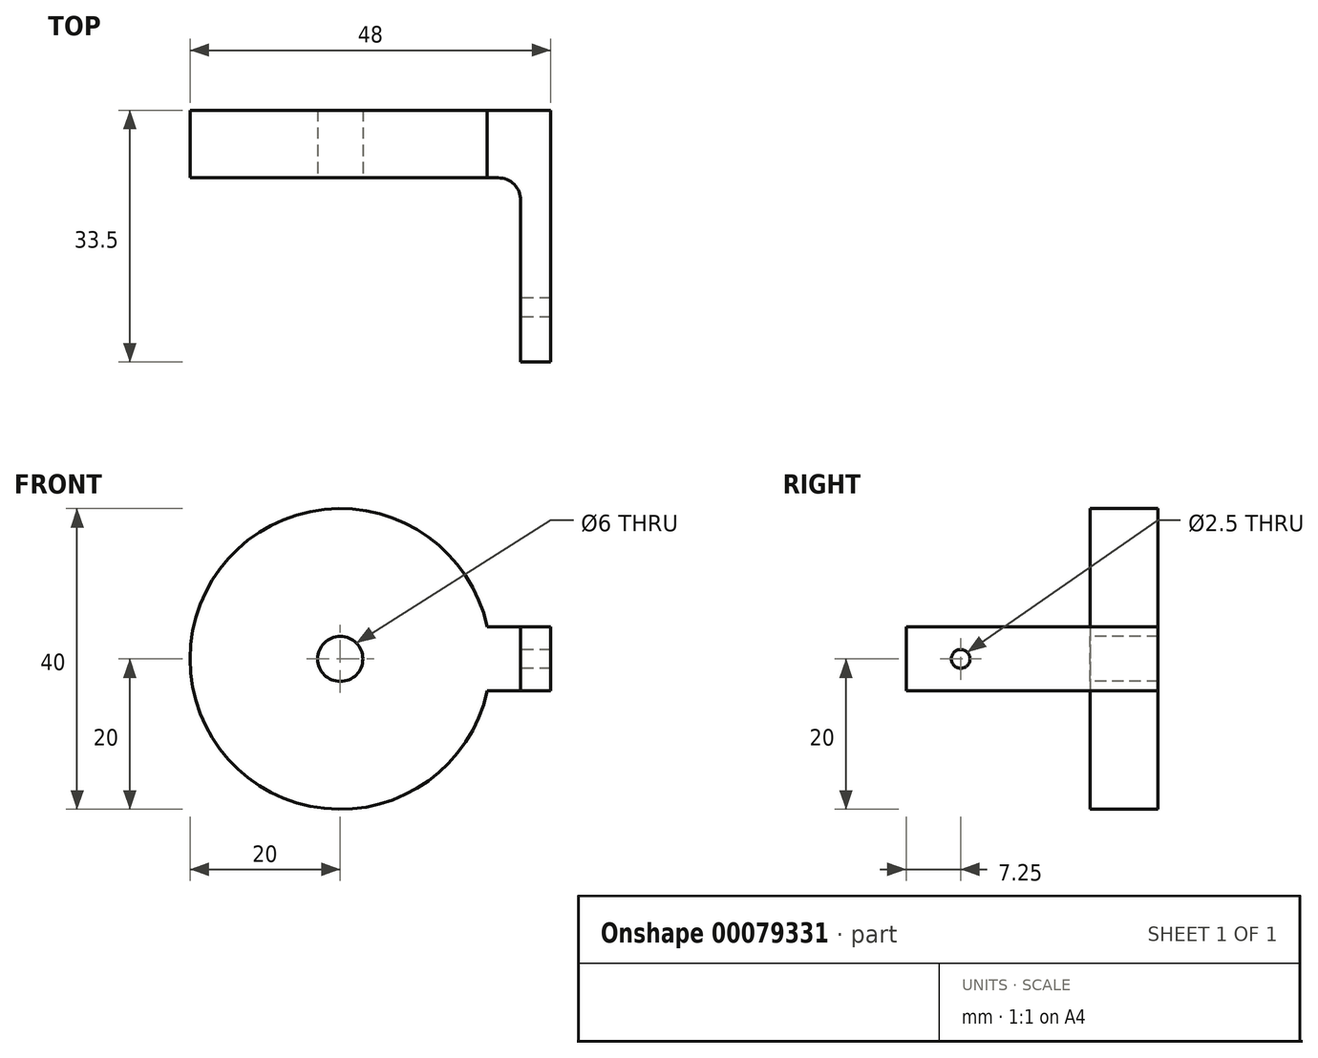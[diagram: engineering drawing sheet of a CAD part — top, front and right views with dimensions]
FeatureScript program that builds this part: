
annotation { "Feature Type Name" : "Feature", "Feature Type Description" : "" }
export const myFeature = defineFeature(function(context is Context, id is Id, definition is map)
    precondition{}
    {
        {
            var Q0;
            Q0=qCreatedBy(makeId("Front.planeOp"),FACE);
            var sketch = newSketch(context, id + "F0", { "sketchPlane" : qUnion([Q0])});
            skCircle(sketch, "E0", {"center": v(0, 0) * mm, "radius": 20 * mm});
            skSolve(sketch);
        }
        {
            var Q0;
            Q0 = qSketchRegion(id + "F0", true);
            extrude(context, id + "F1", {"entities" : qUnion([Q0]), "depth" : 9 * mm});
        }
        {
            var Q0;
            Q0=makeQuery(id+"F1.opExtrude","CAP_FACE",FACE,{"disambiguationData":[OSD([sQuery(id+"F0.wireOp",EDGE,"E0")])],"isStart":false});
            var sketch = newSketch(context, id + "F2", { "sketchPlane" : qUnion([Q0])});
            skCircle(sketch, "E1", {"center": v(0, 0) * mm, "radius": 3 * mm});
            skSolve(sketch);
        }
        {
            var Q0;
            Q0 = qSketchRegion(id + "F2", true);
            extrude(context, id + "F3", {"entities" : qUnion([Q0]), "operationType" : NewBodyOperationType.REMOVE, "endBound" : BoundingType.THROUGH_ALL, "oppositeDirection" : true, "depth" : 25 * mm});
        }
        {
            var Q0;
            Q0=qCreatedBy(makeId("Top.planeOp"),FACE);
            var sketch = newSketch(context, id + "F4", { "sketchPlane" : qUnion([Q0])});
            skLineSegment(sketch, "E2.bottom", {"start": v(20, -9) * mm, "end": v(21, -9) * mm});
            skLineSegment(sketch, "E2.top", {"start": v(20, 0) * mm, "end": v(28, 0) * mm});
            skLineSegment(sketch, "E2.right", {"start": v(28, -9) * mm, "end": v(28, 0) * mm});
            skLineSegment(sketch, "E3.top", {"start": v(28, -33.5) * mm, "end": v(24, -33.5) * mm});
            skLineSegment(sketch, "E3.left", {"start": v(28, -9) * mm, "end": v(28, -33.5) * mm});
            skLineSegment(sketch, "E3.right", {"start": v(24, -12) * mm, "end": v(24, -33.5) * mm});
            skPoint(sketch, "E4.visualSharp", {"position": v(24, -9) * mm});
            skArc(sketch, "E4.filletArc", {"start": v(24, -12) * mm, "mid": v(23.12, -9.88) * mm, "end": v(21, -9) * mm});
            skLineSegment(sketch, "E5.bottom", {"start": v(20, -9) * mm, "end": v(15.48, -9) * mm});
            skLineSegment(sketch, "E5.top", {"start": v(20, 0) * mm, "end": v(15.48, 0) * mm});
            skLineSegment(sketch, "E5.right", {"start": v(15.48, -9) * mm, "end": v(15.48, 0) * mm});
            skSolve(sketch);
        }
        {
            var Q0;
            Q0 = qSketchRegion(id + "F4", true);
            extrude(context, id + "F5", {"entities" : qUnion([Q0]), "operationType" : NewBodyOperationType.ADD, "endBound" : BoundingType.SYMMETRIC, "depth" : 8.5 * mm});
        }
        {
            var Q0;
            Q0=qCreatedBy(makeId("Right.planeOp"),FACE);
            var sketch = newSketch(context, id + "F6", { "sketchPlane" : qUnion([Q0])});
            skLineSegment(sketch, "E6", {"start": v(-26.25, 4.25) * mm, "end": v(-26.25, -4.25) * mm, "construction": true});
            skCircle(sketch, "E7", {"center": v(-26.25, 0) * mm, "radius": 1.25 * mm});
            skSolve(sketch);
        }
        {
            var Q0;
            Q0 = qSketchRegion(id + "F6", true);
            extrude(context, id + "F7", {"entities" : qUnion([Q0]), "operationType" : NewBodyOperationType.REMOVE, "endBound" : BoundingType.THROUGH_ALL, "depth" : 25 * mm});
        }
    });
